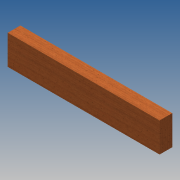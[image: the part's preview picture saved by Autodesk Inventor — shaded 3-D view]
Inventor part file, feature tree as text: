
AUTODESK INVENTOR PART (.ipt)
format: ipt  version: 2013 (Build 170138000, 138)  size: 80,384 bytes
history: native  units: in
note: dims shown in document units (in); Inventor stores cm internally (conversion verified against a paired STEP export)
features: extrude x1, sketch x1
ambient origin geometry x8: Origin, YZ Plane, XZ Plane, XY Plane, X Axis, Y Axis, Z Axis, Center Point
bodies: Solid1 (feature_tree)
feature tree (2):
  extrude  "Extrusion1"  Depth=3.5in
  sketch  "Sketch1"  dims[d0=1.5in d1=3.5in d2=18.0in d3=0.0in]
